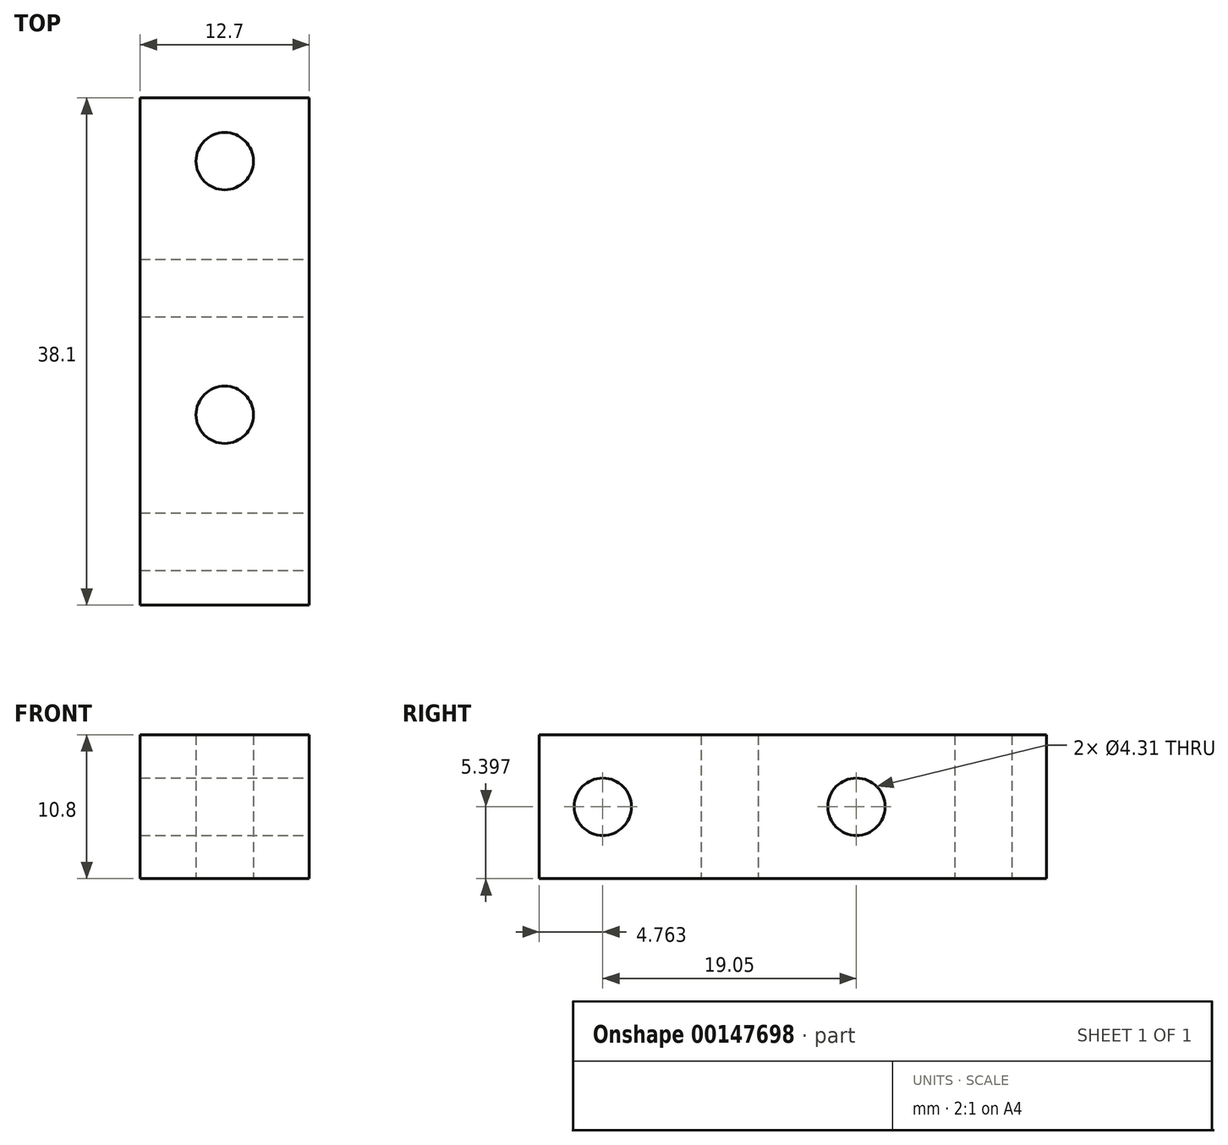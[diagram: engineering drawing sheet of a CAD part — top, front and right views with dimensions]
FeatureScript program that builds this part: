
annotation { "Feature Type Name" : "Feature", "Feature Type Description" : "" }
export const myFeature = defineFeature(function(context is Context, id is Id, definition is map)
    precondition{}
    {
        {
            var Q0;
            Q0=qCreatedBy(makeId("Top.planeOp"),FACE);
            var sketch = newSketch(context, id + "F0", { "sketchPlane" : qUnion([Q0])});
            skLineSegment(sketch, "E0.bottom", {"start": v(0, 0) * mm, "end": v(12.7, 0) * mm});
            skLineSegment(sketch, "E0.top", {"start": v(0, -38.1) * mm, "end": v(12.7, -38.1) * mm});
            skLineSegment(sketch, "E0.left", {"start": v(0, 0) * mm, "end": v(0, -38.1) * mm});
            skLineSegment(sketch, "E0.right", {"start": v(12.7, 0) * mm, "end": v(12.7, -38.1) * mm});
            skLineSegment(sketch, "E1", {"start": v(6.35, 0) * mm, "end": v(6.35, -4.76) * mm, "construction": true});
            skLineSegment(sketch, "E2", {"start": v(6.35, -4.76) * mm, "end": v(6.35, -23.81) * mm, "construction": true});
            skCircle(sketch, "E3", {"center": v(6.35, -4.76) * mm, "radius": 2.15 * mm});
            skCircle(sketch, "E4", {"center": v(6.35, -23.81) * mm, "radius": 2.15 * mm});
            skLineSegment(sketch, "E5", {"start": v(6.35, -23.81) * mm, "end": v(6.35, -38.1) * mm, "construction": true});
            skSolve(sketch);
        }
        {
            var Q0;
            Q0=qSketchRegion(id+"F0",true);
            extrude(context, id + "F1", {"entities" : qUnion([Q0]), "depth" : 10.8 * mm});
        }
        {
            var Q0;
            Q0=makeQuery(id+"F1.opExtrude","SWEPT_FACE",FACE,{"disambiguationData":[OSD([sQuery(id+"F0.wireOp",EDGE,"E0.right")])]});
            var sketch = newSketch(context, id + "F2", { "sketchPlane" : qUnion([Q0])});
            skLineSegment(sketch, "E6", {"start": v(-38.1, 5.4) * mm, "end": v(-33.34, 5.4) * mm, "construction": true});
            skLineSegment(sketch, "E7", {"start": v(0, 5.4) * mm, "end": v(-4.76, 5.4) * mm, "construction": true});
            skLineSegment(sketch, "E8", {"start": v(-4.76, 5.4) * mm, "end": v(-23.81, 5.4) * mm, "construction": true});
            skLineSegment(sketch, "E9", {"start": v(-4.76, 5.4) * mm, "end": v(-4.76, 10.8) * mm, "construction": true});
            skLineSegment(sketch, "E10", {"start": v(-23.81, 5.4) * mm, "end": v(-23.81, 10.8) * mm, "construction": true});
            skCircle(sketch, "E11", {"center": v(-33.34, 5.4) * mm, "radius": 2.15 * mm});
            skCircle(sketch, "E12", {"center": v(-14.29, 5.4) * mm, "radius": 2.15 * mm});
            skSolve(sketch);
        }
        {
            var Q0;
            Q0=qSketchRegion(id+"F2",true);
            var Q1;
            Q1=makeQuery(id+"F1.opExtrude","SWEPT_FACE",FACE,{"disambiguationData":[OSD([sQuery(id+"F0.wireOp",EDGE,"E0.left")])]});
            extrude(context, id + "F3", {"entities" : qUnion([Q0]), "operationType" : NewBodyOperationType.REMOVE, "endBound" : BoundingType.UP_TO_SURFACE, "oppositeDirection" : true, "endBoundEntityFace" : qUnion([Q1]), "depth" : 25.4 * mm});
        }
    });
